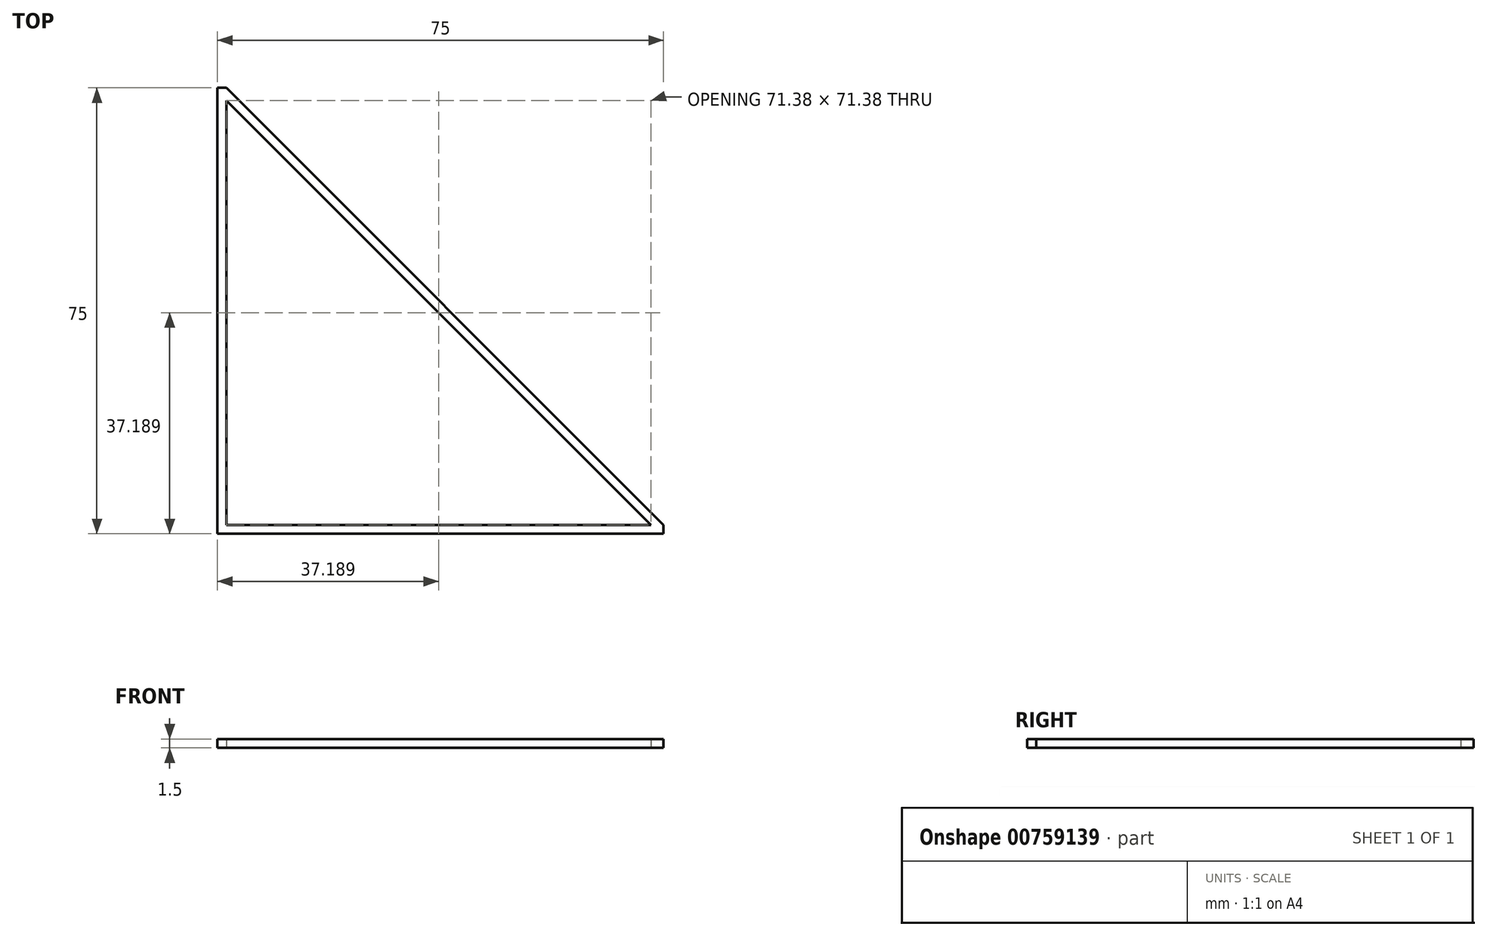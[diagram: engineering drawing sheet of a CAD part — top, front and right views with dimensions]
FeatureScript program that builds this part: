
annotation { "Feature Type Name" : "Feature", "Feature Type Description" : "" }
export const myFeature = defineFeature(function(context is Context, id is Id, definition is map)
    precondition{}
    {
        {
            var Q0;
            Q0=qCreatedBy(makeId("Top.planeOp"),FACE);
            var sketch = newSketch(context, id + "F0", { "sketchPlane" : qUnion([Q0])});
            skLineSegment(sketch, "E0.bottom", {"start": v(0, 75) * mm, "end": v(1.5, 75) * mm});
            skLineSegment(sketch, "E0.top", {"start": v(0, 0) * mm, "end": v(1.5, 0) * mm});
            skLineSegment(sketch, "E0.left", {"start": v(0, 75) * mm, "end": v(0, 0) * mm});
            skLineSegment(sketch, "E0.right", {"start": v(1.5, 72.88) * mm, "end": v(1.5, 1.5) * mm});
            skLineSegment(sketch, "E1.bottom", {"start": v(0, 0) * mm, "end": v(75, 0) * mm});
            skLineSegment(sketch, "E1.top", {"start": v(1.5, 1.5) * mm, "end": v(72.88, 1.5) * mm});
            skLineSegment(sketch, "E1.left", {"start": v(0, 0) * mm, "end": v(0, 1.5) * mm});
            skLineSegment(sketch, "E1.right", {"start": v(75, 0) * mm, "end": v(75, 1.5) * mm});
            skLineSegment(sketch, "E2", {"start": v(1.5, 75) * mm, "end": v(75, 1.5) * mm});
            skLineSegment(sketch, "E3", {"start": v(1.5, 72.88) * mm, "end": v(72.88, 1.5) * mm});
            skSolve(sketch);
        }
        {
            var Q0;
            Q0 = qSketchRegion(id + "F0", true);
            extrude(context, id + "F1", {"entities" : qUnion([Q0]), "depth" : 1.5 * mm, "offsetDistance" : 25 * mm});
        }
    });
